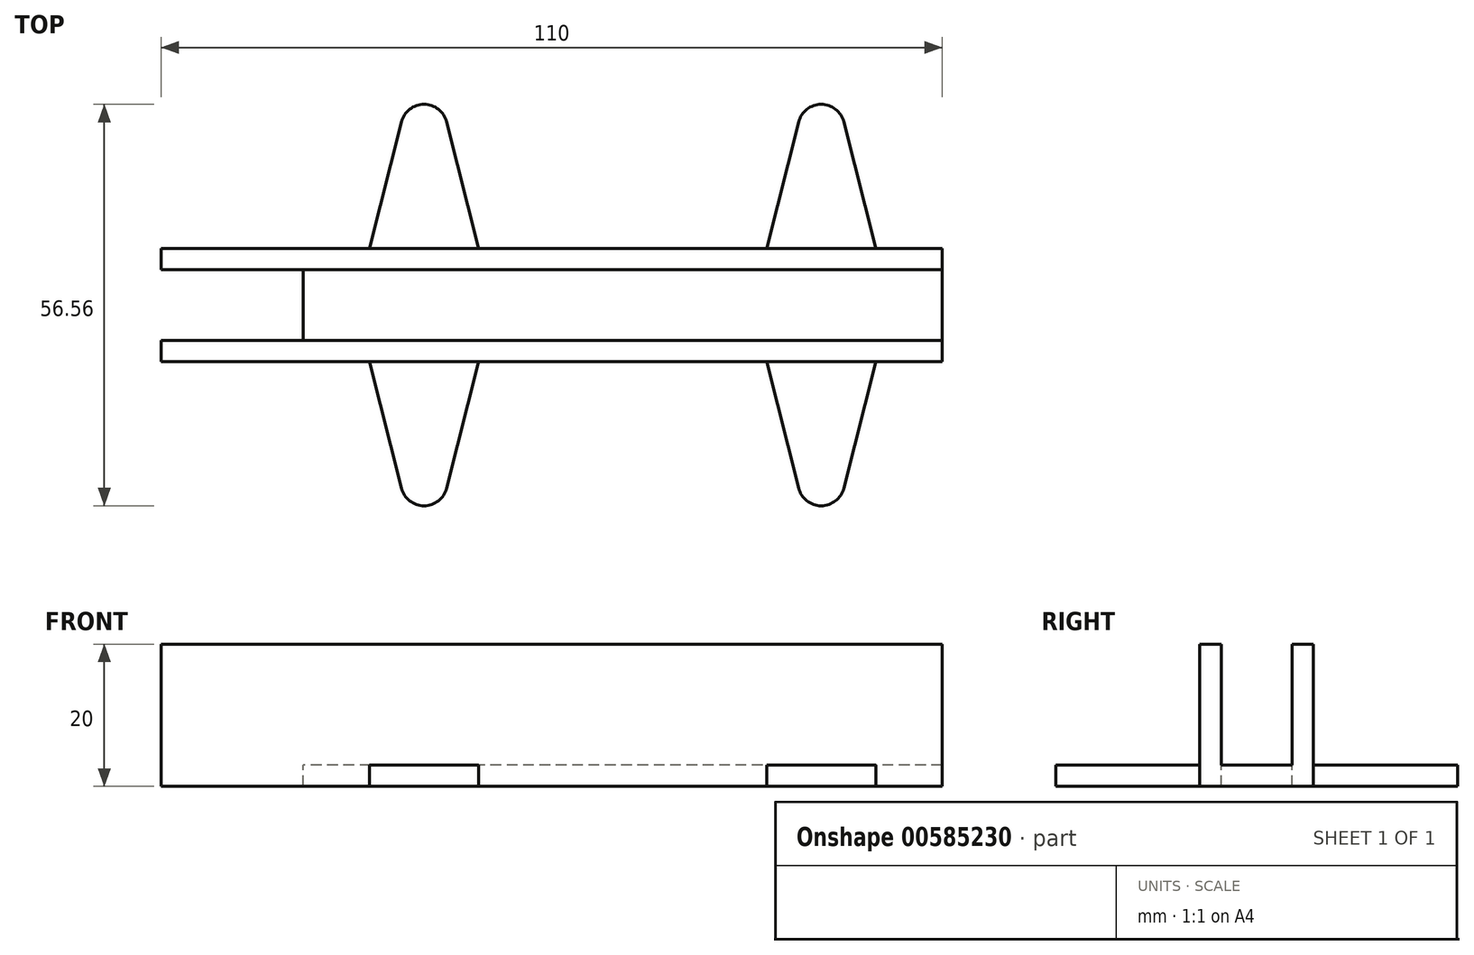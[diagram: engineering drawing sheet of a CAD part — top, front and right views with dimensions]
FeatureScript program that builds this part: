
annotation { "Feature Type Name" : "Feature", "Feature Type Description" : "" }
export const myFeature = defineFeature(function(context is Context, id is Id, definition is map)
    precondition{}
    {
        {
            var Q0;
            Q0=qCreatedBy(makeId("Top.planeOp"),FACE);
            var sketch = newSketch(context, id + "F0", { "sketchPlane" : qUnion([Q0])});
            skLineSegment(sketch, "E0.bottom", {"start": v(55, -8) * mm, "end": v(-55, -8) * mm});
            skLineSegment(sketch, "E0.top", {"start": v(55, 8) * mm, "end": v(-55, 8) * mm});
            skLineSegment(sketch, "E0.left", {"start": v(55, -8) * mm, "end": v(55, 8) * mm});
            skLineSegment(sketch, "E0.right", {"start": v(-55, -8) * mm, "end": v(-55, 8) * mm});
            skPoint(sketch, "E0.middle", {"position": v(0, 0) * mm});
            skLineSegment(sketch, "E1.bottom", {"start": v(55, -5) * mm, "end": v(-55, -5) * mm});
            skLineSegment(sketch, "E1.top", {"start": v(55, 5) * mm, "end": v(-55, 5) * mm});
            skLineSegment(sketch, "E1.left", {"start": v(55, -5) * mm, "end": v(55, 5) * mm});
            skLineSegment(sketch, "E1.right", {"start": v(-55, -5) * mm, "end": v(-55, 5) * mm});
            skSolve(sketch);
        }
        {
            var Q0;
            Q0=makeQuery(id+"F0.imprint","IMPRINT",FACE,{"disambiguationData":[TD([[makeQuery(id+"F0.imprint","IMPRINT",EDGE,{"derivedFrom":sQuery(id+"F0.wireOp",EDGE,"E1.bottom")}),-1.0]])]});
            extrude(context, id + "F1", {"entities" : qUnion([Q0]), "depth" : 3 * mm, "offsetDistance" : 25 * mm});
        }
        {
            var Q0;
            Q0=makeQuery(id+"F1.opExtrude","CAP_FACE",FACE,{"disambiguationData":[OSD([sQuery(id+"F0.wireOp",EDGE,"E1.bottom"),sQuery(id+"F0.wireOp",EDGE,"E1.top"),sQuery(id+"F0.wireOp",EDGE,"E1.left"),sQuery(id+"F0.wireOp",EDGE,"E1.right")])],"isStart":false});
            var sketch = newSketch(context, id + "F2", { "sketchPlane" : qUnion([Q0])});
            skLineSegment(sketch, "E2.bottom", {"start": v(-55, 5) * mm, "end": v(-35, 5) * mm});
            skLineSegment(sketch, "E2.top", {"start": v(-55, -5) * mm, "end": v(-35, -5) * mm});
            skLineSegment(sketch, "E2.left", {"start": v(-55, 5) * mm, "end": v(-55, -5) * mm});
            skLineSegment(sketch, "E2.right", {"start": v(-35, 5) * mm, "end": v(-35, -5) * mm});
            skSolve(sketch);
        }
        {
            var Q0;
            {var subQ0=sQuery(id+"F0.wireOp",EDGE,"E0.bottom");Q0=makeQuery(id+"F0.imprint","IMPRINT",FACE,{"disambiguationData":[TD([[makeQuery(id+"F0.imprint","IMPRINT",EDGE,{"derivedFrom":subQ0}),-1.0]])]});}
            var Q1;
            {var subQ0=sQuery(id+"F0.wireOp",EDGE,"E0.top");Q1=makeQuery(id+"F0.imprint","IMPRINT",FACE,{"disambiguationData":[TD([[makeQuery(id+"F0.imprint","IMPRINT",EDGE,{"derivedFrom":subQ0}),1.0]])]});}
            extrude(context, id + "F3", {"entities" : qUnion([Q0, Q1]), "operationType" : NewBodyOperationType.ADD, "depth" : 20 * mm, "offsetDistance" : 25 * mm});
        }
        {
            var Q0;
            Q0=makeQuery(id+"F2.imprint","IMPRINT",FACE,{"disambiguationData":[TD([[makeQuery(id+"F2.imprint","IMPRINT",EDGE,{"derivedFrom":sQuery(id+"F2.wireOp",EDGE,"E2.bottom")}),1.0]])]});
            extrude(context, id + "F4", {"entities" : qUnion([Q0]), "operationType" : NewBodyOperationType.REMOVE, "endBound" : BoundingType.UP_TO_NEXT, "oppositeDirection" : true, "depth" : 25 * mm, "offsetDistance" : 25 * mm});
        }
        {
            var Q0;
            Q0=makeQuery(id+"F1.opExtrude","CAP_FACE",FACE,{"disambiguationData":[OSD([sQuery(id+"F0.wireOp",EDGE,"E1.bottom"),sQuery(id+"F0.wireOp",EDGE,"E1.top"),sQuery(id+"F0.wireOp",EDGE,"E1.left"),sQuery(id+"F0.wireOp",EDGE,"E1.right")])],"isStart":false});
            var sketch = newSketch(context, id + "F5", { "sketchPlane" : qUnion([Q0])});
            skLineSegment(sketch, "E3", {"start": v(-26.4, -5) * mm, "end": v(-21.14, -25.8) * mm});
            skLineSegment(sketch, "E4", {"start": v(-9.54, -5) * mm, "end": v(-14.79, -25.8) * mm});
            skArc(sketch, "E5", {"start": v(-21.14, -25.8) * mm, "mid": v(-17.96, -28.28) * mm, "end": v(-14.79, -25.8) * mm});
            skLineSegment(sketch, "E6", {"start": v(10, -5) * mm, "end": v(10, -36.19) * mm, "construction": true});
            skPoint(sketch, "E6.endSnap0", {"position": v(10, 5) * mm});
            skLineSegment(sketch, "E7.MirrorCS", {"start": v(29.54, -5) * mm, "end": v(34.79, -25.8) * mm});
            skArc(sketch, "E8.MirrorCS", {"start": v(41.14, -25.8) * mm, "mid": v(37.96, -28.28) * mm, "end": v(34.79, -25.8) * mm});
            skLineSegment(sketch, "E9.MirrorCS", {"start": v(46.4, -5) * mm, "end": v(41.14, -25.8) * mm});
            skLineSegment(sketch, "E10.MirrorCS", {"start": v(-26.4, 5) * mm, "end": v(-21.14, 25.8) * mm});
            skArc(sketch, "E11.MirrorCS", {"start": v(-21.14, 25.8) * mm, "mid": v(-17.96, 28.28) * mm, "end": v(-14.79, 25.8) * mm});
            skLineSegment(sketch, "E12.MirrorCS", {"start": v(-9.54, 5) * mm, "end": v(-14.79, 25.8) * mm});
            skLineSegment(sketch, "E13.MirrorCS", {"start": v(29.54, 5) * mm, "end": v(34.79, 25.8) * mm});
            skArc(sketch, "E14.MirrorCS", {"start": v(41.14, 25.8) * mm, "mid": v(37.96, 28.28) * mm, "end": v(34.79, 25.8) * mm});
            skLineSegment(sketch, "E15.MirrorCS", {"start": v(46.4, 5) * mm, "end": v(41.14, 25.8) * mm});
            skLineSegment(sketch, "E16", {"start": v(-26.4, -5) * mm, "end": v(-9.54, -5) * mm});
            skLineSegment(sketch, "E17.MirrorCS", {"start": v(46.4, -5) * mm, "end": v(29.54, -5) * mm});
            skLineSegment(sketch, "E18.MirrorCS", {"start": v(-26.4, 5) * mm, "end": v(-9.54, 5) * mm});
            skLineSegment(sketch, "E19.MirrorCS", {"start": v(46.4, 5) * mm, "end": v(29.54, 5) * mm});
            skSolve(sketch);
        }
        {
            var Q0;
            Q0 = qSketchRegion(id + "F5", true);
            var Q1;
            {var subQ0=sQuery(id+"F0.wireOp",EDGE,"E1.top");var subQ1=sQuery(id+"F0.wireOp",EDGE,"E0.right");var subQ2=sQuery(id+"F0.wireOp",EDGE,"E0.left");var subQ3=sQuery(id+"F0.wireOp",EDGE,"E1.bottom");Q1=makeQuery(id+"F3.boolean.opBoolean","MERGE",FACE,{"derivedFrom":[makeQuery(id+"F1.opExtrude","CAP_FACE",FACE,{"disambiguationData":[OSD([subQ3,subQ0,sQuery(id+"F0.wireOp",EDGE,"E1.left"),sQuery(id+"F0.wireOp",EDGE,"E1.right")])],"isStart":true}),makeQuery(id+"F3.opExtrude","CAP_FACE",FACE,{"disambiguationData":[OSD([sQuery(id+"F0.wireOp",EDGE,"E0.bottom"),subQ2,subQ1,subQ3])],"isStart":true}),makeQuery(id+"F3.opExtrude","CAP_FACE",FACE,{"disambiguationData":[OSD([sQuery(id+"F0.wireOp",EDGE,"E0.top"),subQ2,subQ1,subQ0])],"isStart":true})]});}
            extrude(context, id + "F6", {"entities" : qUnion([Q0]), "operationType" : NewBodyOperationType.ADD, "endBound" : BoundingType.UP_TO_SURFACE, "oppositeDirection" : true, "depth" : 25 * mm, "endBoundEntityFace" : qUnion([Q1]), "offsetDistance" : 25 * mm});
        }
    });
